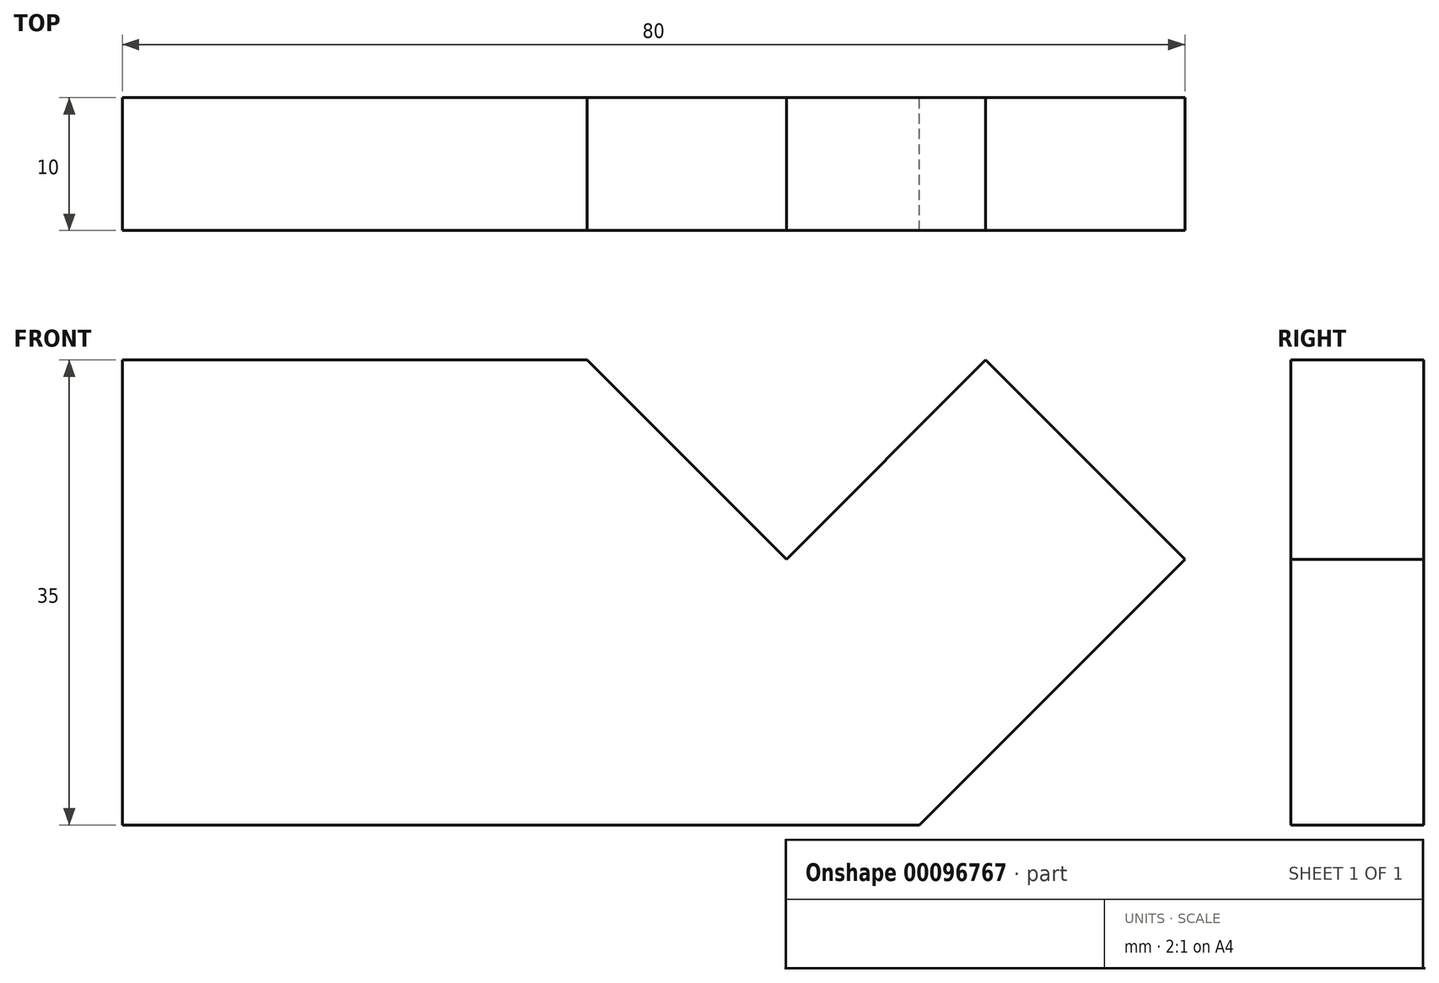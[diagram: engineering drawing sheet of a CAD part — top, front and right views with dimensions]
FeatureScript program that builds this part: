
annotation { "Feature Type Name" : "Feature", "Feature Type Description" : "" }
export const myFeature = defineFeature(function(context is Context, id is Id, definition is map)
    precondition{}
    {
        {
            var Q0;
            Q0=qCreatedBy(makeId("Front.planeOp"),FACE);
            var sketch = newSketch(context, id + "F0", { "sketchPlane" : qUnion([Q0])});
            skLineSegment(sketch, "E0", {"start": v(0, 1577.6) * mm, "end": v(13.72, 1577.6) * mm});
            skLineSegment(sketch, "E1", {"start": v(0, 0) * mm, "end": v(0, 35) * mm});
            skLineSegment(sketch, "E2", {"start": v(65, 35) * mm, "end": v(50, 20) * mm});
            skLineSegment(sketch, "E3", {"start": v(65, 35) * mm, "end": v(80, 20) * mm});
            skLineSegment(sketch, "E4", {"start": v(80, 20) * mm, "end": v(60, 0) * mm});
            skLineSegment(sketch, "E5", {"start": v(60, 0) * mm, "end": v(0, 0) * mm});
            skLineSegment(sketch, "E6", {"start": v(50, 20) * mm, "end": v(35, 35) * mm});
            skLineSegment(sketch, "E7", {"start": v(0, 35) * mm, "end": v(35, 35) * mm});
            skSolve(sketch);
        }
        {
            var Q0;
            Q0 = qSketchRegion(id + "F0", true);
            extrude(context, id + "F1", {"entities" : qUnion([Q0]), "depth" : 10 * mm});
        }
    });
